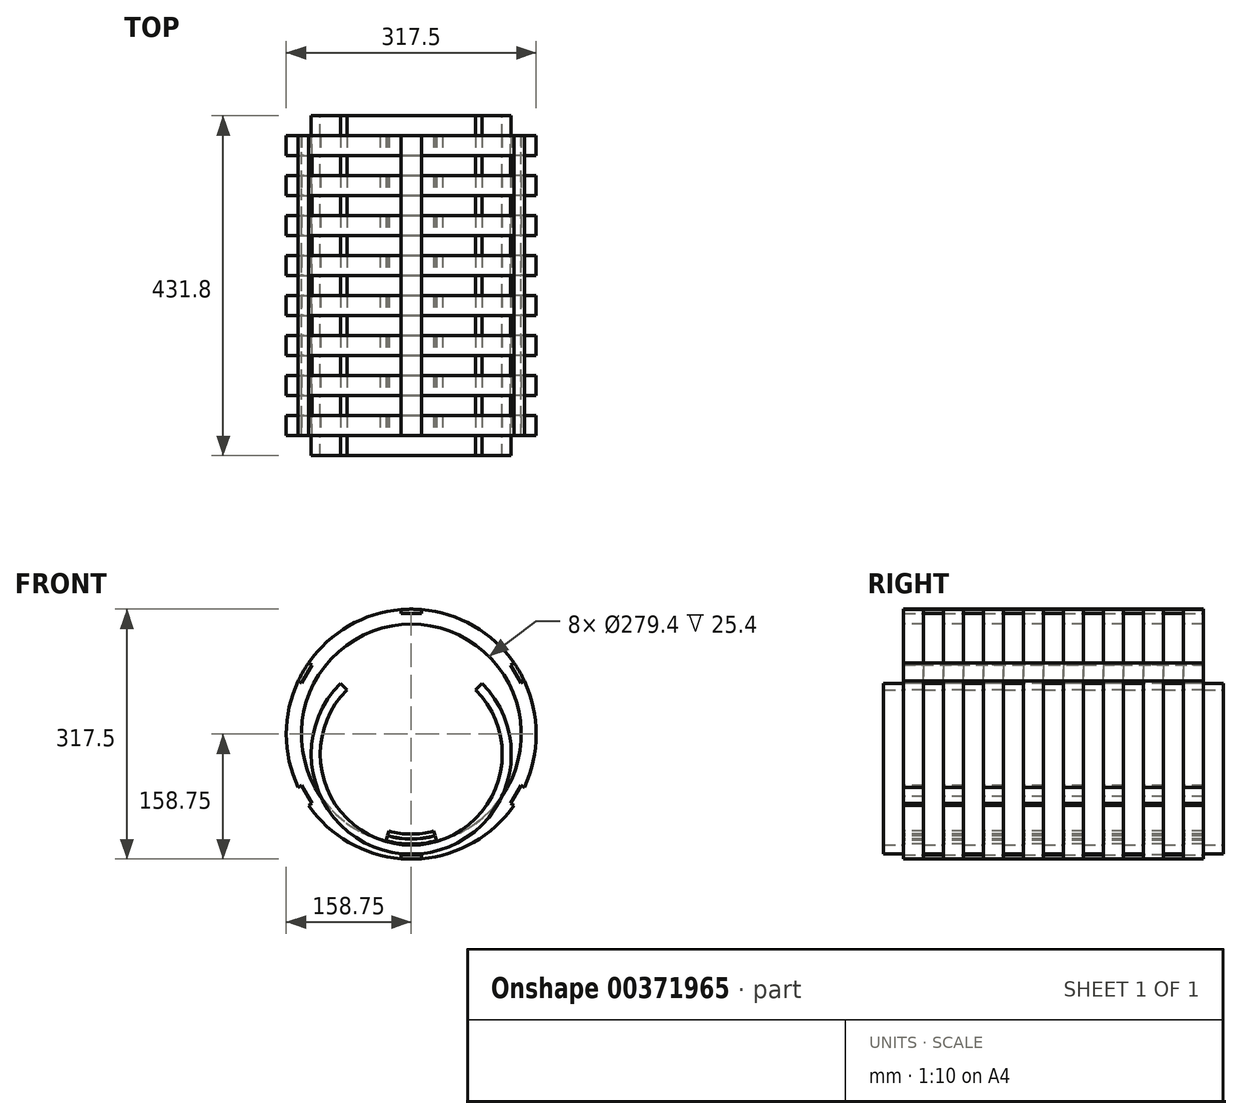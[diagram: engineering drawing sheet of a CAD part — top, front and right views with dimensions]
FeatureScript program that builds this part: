
annotation { "Feature Type Name" : "Feature", "Feature Type Description" : "" }
export const myFeature = defineFeature(function(context is Context, id is Id, definition is map)
    precondition{}
    {
        {
            var Q0;
            Q0=qCreatedBy(makeId("Front.planeOp"),FACE);
            var sketch = newSketch(context, id + "F0", { "sketchPlane" : qUnion([Q0])});
            skCircle(sketch, "E0", {"center": v(0, 0) * mm, "radius": 114.3 * mm});
            skCircle(sketch, "E1", {"center": v(0, 0) * mm, "radius": 107.95 * mm});
            skCircle(sketch, "E2", {"center": v(0, 0) * mm, "radius": 107.63 * mm});
            skCircle(sketch, "E3", {"center": v(0, 0) * mm, "radius": 101.6 * mm});
            skLineSegment(sketch, "E4", {"start": v(-28.5, -97.52) * mm, "end": v(-30.18, -103.31) * mm});
            skLineSegment(sketch, "E5", {"start": v(-30.27, -103.62) * mm, "end": v(-32.05, -109.71) * mm});
            skLineSegment(sketch, "E6", {"start": v(28.5, -97.52) * mm, "end": v(30.18, -103.31) * mm});
            skLineSegment(sketch, "E7", {"start": v(30.27, -103.62) * mm, "end": v(32.05, -109.71) * mm});
            skCircle(sketch, "E8", {"center": v(0, 0) * mm, "radius": 115.57 * mm});
            skCircle(sketch, "E9", {"center": v(0, 0) * mm, "radius": 127 * mm});
            skLineSegment(sketch, "E10", {"start": v(0, 0) * mm, "end": v(0, 68.07) * mm});
            skLineSegment(sketch, "E11", {"start": v(0, 0) * mm, "end": v(89.8, 89.8) * mm});
            skLineSegment(sketch, "E12", {"start": v(0, 0) * mm, "end": v(-89.8, 89.8) * mm});
            skCircle(sketch, "E13", {"center": v(0, 0) * mm, "radius": 139.7 * mm});
            skCircle(sketch, "E14", {"center": v(0, 0) * mm, "radius": 158.75 * mm});
            skLineSegment(sketch, "E15.bottom", {"start": v(13.23, 153.33) * mm, "end": v(-13.23, 153.33) * mm});
            skPoint(sketch, "E15.middle", {"position": v(0, 158.75) * mm});
            skArc(sketch, "E16", {"start": v(13.23, 158.2) * mm, "mid": v(0, 158.75) * mm, "end": v(-13.23, 158.2) * mm});
            skLineSegment(sketch, "E17", {"start": v(-13.23, 158.2) * mm, "end": v(-13.23, 153.33) * mm});
            skLineSegment(sketch, "E18", {"start": v(-13.23, 153.33) * mm, "end": v(13.23, 153.33) * mm});
            skLineSegment(sketch, "E19", {"start": v(13.23, 153.33) * mm, "end": v(13.23, 158.2) * mm});
            skLineSegment(sketch, "E20.1.0", {"start": v(-130.39, -90.56) * mm, "end": v(-126.17, -88.12) * mm});
            skLineSegment(sketch, "E20.1.1", {"start": v(-126.17, -88.12) * mm, "end": v(-139.4, -65.2) * mm});
            skLineSegment(sketch, "E20.1.2", {"start": v(-139.4, -65.2) * mm, "end": v(-143.62, -67.64) * mm});
            skLineSegment(sketch, "E20.2.0", {"start": v(143.62, -67.64) * mm, "end": v(139.4, -65.2) * mm});
            skLineSegment(sketch, "E20.2.1", {"start": v(139.4, -65.2) * mm, "end": v(126.17, -88.12) * mm});
            skLineSegment(sketch, "E20.2.2", {"start": v(126.17, -88.12) * mm, "end": v(130.39, -90.56) * mm});
            skArc(sketch, "E21.1.0", {"start": v(-130.39, 90.56) * mm, "mid": v(-137.48, 79.38) * mm, "end": v(-143.62, 67.64) * mm});
            skLineSegment(sketch, "E21.1.1", {"start": v(-126.17, 88.12) * mm, "end": v(-130.39, 90.56) * mm});
            skLineSegment(sketch, "E21.1.2", {"start": v(-139.4, 65.2) * mm, "end": v(-126.17, 88.12) * mm});
            skLineSegment(sketch, "E21.1.3", {"start": v(-143.62, 67.64) * mm, "end": v(-139.4, 65.2) * mm});
            skArc(sketch, "E21.2.0", {"start": v(-143.62, -67.64) * mm, "mid": v(-137.48, -79.38) * mm, "end": v(-130.39, -90.56) * mm});
            skArc(sketch, "E21.3.0", {"start": v(-13.23, -158.2) * mm, "mid": v(0, -158.75) * mm, "end": v(13.23, -158.2) * mm});
            skLineSegment(sketch, "E21.3.1", {"start": v(-13.23, -153.33) * mm, "end": v(-13.23, -158.2) * mm});
            skLineSegment(sketch, "E21.3.2", {"start": v(13.23, -153.33) * mm, "end": v(-13.23, -153.33) * mm});
            skLineSegment(sketch, "E21.3.3", {"start": v(13.23, -158.2) * mm, "end": v(13.23, -153.33) * mm});
            skArc(sketch, "E21.4.0", {"start": v(130.39, -90.56) * mm, "mid": v(137.48, -79.38) * mm, "end": v(143.62, -67.64) * mm});
            skArc(sketch, "E21.5.0", {"start": v(143.62, 67.64) * mm, "mid": v(137.48, 79.38) * mm, "end": v(130.39, 90.56) * mm});
            skLineSegment(sketch, "E21.5.1", {"start": v(139.4, 65.2) * mm, "end": v(143.62, 67.64) * mm});
            skLineSegment(sketch, "E21.5.2", {"start": v(126.17, 88.12) * mm, "end": v(139.4, 65.2) * mm});
            skLineSegment(sketch, "E21.5.3", {"start": v(130.39, 90.56) * mm, "end": v(126.17, 88.12) * mm});
            skCircle(sketch, "E22", {"center": v(0, 0) * mm, "radius": 25.4 * mm});
            skArc(sketch, "E23", {"start": v(-114.96, -53.97) * mm, "mid": v(0, -114.3) * mm, "end": v(114.96, -53.97) * mm});
            skSolve(sketch);
        }
        {
            var Q0;
            {var subQ0=sQuery(id+"F0.wireOp",EDGE,"E4");Q0=makeQuery(id+"F0.imprint","IMPRINT",FACE,{"disambiguationData":[TD([[makeQuery(id+"F0.imprint","IMPRINT",EDGE,{"derivedFrom":subQ0}),1.0]])]});}
            extrude(context, id + "F1", {"entities" : qUnion([Q0]), "oppositeDirection" : true, "depth" : 25.4 * mm, "offsetDistance" : 25.4 * mm});
        }
        {
            var Q0;
            {var subQ0=sQuery(id+"F0.wireOp",EDGE,"E5");Q0=makeQuery(id+"F0.imprint","IMPRINT",FACE,{"disambiguationData":[TD([[makeQuery(id+"F0.imprint","IMPRINT",EDGE,{"derivedFrom":subQ0}),1.0]])]});}
            extrude(context, id + "F2", {"entities" : qUnion([Q0]), "oppositeDirection" : true, "depth" : 25.4 * mm, "offsetDistance" : 25.4 * mm});
        }
        {
            var Q0;
            {var subQ0=sQuery(id+"F0.wireOp",EDGE,"E12");var subQ1=sQuery(id+"F0.wireOp",EDGE,"E8");var subQ2=makeQuery(id+"F0.imprint","INTERSECT",VERTEX,{"derivedFrom":[subQ1,subQ0]});Q0=makeQuery(id+"F0.imprint","IMPRINT",FACE,{"disambiguationData":[TD([[makeQuery(id+"F0.imprint","IMPRINT",EDGE,{"disambiguationData":[TD([[subQ2,-1.0]])],"derivedFrom":subQ1}),-1.0]])]});}
            var Q1;
            {var subQ0=sQuery(id+"F0.wireOp",EDGE,"E11");var subQ1=sQuery(id+"F0.wireOp",EDGE,"E8");var subQ2=makeQuery(id+"F0.imprint","INTERSECT",VERTEX,{"derivedFrom":[subQ1,subQ0]});Q1=makeQuery(id+"F0.imprint","IMPRINT",FACE,{"disambiguationData":[TD([[makeQuery(id+"F0.imprint","IMPRINT",EDGE,{"disambiguationData":[TD([[subQ2,1.0]])],"derivedFrom":subQ1}),-1.0]])]});}
            extrude(context, id + "F3", {"entities" : qUnion([Q0, Q1]), "oppositeDirection" : true, "depth" : 25.4 * mm, "offsetDistance" : 25.4 * mm});
        }
        {
            var Q0;
            Q0=makeQuery(id+"F0.imprint","IMPRINT",FACE,{"disambiguationData":[TD([[makeQuery(id+"F0.imprint","IMPRINT",EDGE,{"derivedFrom":sQuery(id+"F0.wireOp",EDGE,"E13")}),-1.0]])]});
            extrude(context, id + "F4", {"entities" : qUnion([Q0]), "oppositeDirection" : true, "depth" : 25.4 * mm, "offsetDistance" : 25.4 * mm});
        }
        {
            var Q0;
            Q0=makeQuery(id+"F4.opExtrude","SWEPT_BODY",BODY,{"disambiguationData":[OSD([sQuery(id+"F0.wireOp",EDGE,"E13"),sQuery(id+"F0.wireOp",EDGE,"E14"),sQuery(id+"F0.wireOp",EDGE,"E17"),sQuery(id+"F0.wireOp",EDGE,"E18"),sQuery(id+"F0.wireOp",EDGE,"E19"),sQuery(id+"F0.wireOp",EDGE,"E21.1.1"),sQuery(id+"F0.wireOp",EDGE,"E21.1.2"),sQuery(id+"F0.wireOp",EDGE,"E21.1.3"),sQuery(id+"F0.wireOp",EDGE,"E20.1.2"),sQuery(id+"F0.wireOp",EDGE,"E20.1.1"),sQuery(id+"F0.wireOp",EDGE,"E20.1.0"),sQuery(id+"F0.wireOp",EDGE,"E21.3.1"),sQuery(id+"F0.wireOp",EDGE,"E21.3.2"),sQuery(id+"F0.wireOp",EDGE,"E21.3.3"),sQuery(id+"F0.wireOp",EDGE,"E20.2.2"),sQuery(id+"F0.wireOp",EDGE,"E20.2.1"),sQuery(id+"F0.wireOp",EDGE,"E20.2.0"),sQuery(id+"F0.wireOp",EDGE,"E21.5.1"),sQuery(id+"F0.wireOp",EDGE,"E21.5.2"),sQuery(id+"F0.wireOp",EDGE,"E21.5.3")])]});
            transform(context, id + "F5", {"entities" : qUnion([Q0]), "transformType" : TransformType.TRANSLATION_3D, "dx" : 0 * mm, "dy" : 0 * mm, "dz" : 25.4 * mm, "makeCopy" : false});
        }
        {
            var Q0;
            {var subQ0=sQuery(id+"F0.wireOp",EDGE,"E12");var subQ1=sQuery(id+"F0.wireOp",EDGE,"E8");var subQ2=makeQuery(id+"F0.imprint","INTERSECT",VERTEX,{"derivedFrom":[subQ1,subQ0]});Q0=makeQuery(id+"F0.imprint","IMPRINT",FACE,{"disambiguationData":[TD([[makeQuery(id+"F0.imprint","IMPRINT",EDGE,{"disambiguationData":[TD([[subQ2,-1.0]])],"derivedFrom":subQ1}),-1.0]])]});}
            var Q1;
            {var subQ0=sQuery(id+"F0.wireOp",EDGE,"E11");var subQ1=sQuery(id+"F0.wireOp",EDGE,"E8");var subQ2=makeQuery(id+"F0.imprint","INTERSECT",VERTEX,{"derivedFrom":[subQ1,subQ0]});Q1=makeQuery(id+"F0.imprint","IMPRINT",FACE,{"disambiguationData":[TD([[makeQuery(id+"F0.imprint","IMPRINT",EDGE,{"disambiguationData":[TD([[subQ2,1.0]])],"derivedFrom":subQ1}),-1.0]])]});}
            var Q2;
            {var subQ0=sQuery(id+"F0.wireOp",EDGE,"E23");var subQ1=sQuery(id+"F0.wireOp",EDGE,"E8");var subQ2=makeQuery(id+"F0.imprint","INTERSECT",VERTEX,{"disambiguationData":[OD(0.0)],"derivedFrom":[subQ1,subQ0]});Q2=makeQuery(id+"F0.imprint","IMPRINT",FACE,{"disambiguationData":[TD([[makeQuery(id+"F0.imprint","IMPRINT",EDGE,{"disambiguationData":[TD([[subQ2,-1.0]])],"derivedFrom":subQ1}),-1.0]])]});}
            extrude(context, id + "F6", {"entities" : qUnion([Q0, Q1, Q2]), "depth" : 25.4 * mm, "offsetDistance" : 25.4 * mm});
        }
        {
            var Q0;
            {var subQ0=sQuery(id+"F0.wireOp",EDGE,"E21.5.1");Q0=makeQuery(id+"F0.imprint","IMPRINT",FACE,{"disambiguationData":[TD([[makeQuery(id+"F0.imprint","IMPRINT",EDGE,{"derivedFrom":subQ0}),1.0]])]});}
            var Q1;
            {var subQ0=sQuery(id+"F0.wireOp",EDGE,"E17");Q1=makeQuery(id+"F0.imprint","IMPRINT",FACE,{"disambiguationData":[TD([[makeQuery(id+"F0.imprint","IMPRINT",EDGE,{"derivedFrom":subQ0}),1.0]])]});}
            var Q2;
            {var subQ0=sQuery(id+"F0.wireOp",EDGE,"E21.1.1");Q2=makeQuery(id+"F0.imprint","IMPRINT",FACE,{"disambiguationData":[TD([[makeQuery(id+"F0.imprint","IMPRINT",EDGE,{"derivedFrom":subQ0}),1.0]])]});}
            var Q3;
            {var subQ0=sQuery(id+"F0.wireOp",EDGE,"E21.3.1");Q3=makeQuery(id+"F0.imprint","IMPRINT",FACE,{"disambiguationData":[TD([[makeQuery(id+"F0.imprint","IMPRINT",EDGE,{"derivedFrom":subQ0}),1.0]])]});}
            var Q4;
            {var subQ0=sQuery(id+"F0.wireOp",EDGE,"E20.1.2");Q4=makeQuery(id+"F0.imprint","IMPRINT",FACE,{"disambiguationData":[TD([[makeQuery(id+"F0.imprint","IMPRINT",EDGE,{"derivedFrom":subQ0}),1.0]])]});}
            var Q5;
            {var subQ0=sQuery(id+"F0.wireOp",EDGE,"E20.2.2");Q5=makeQuery(id+"F0.imprint","IMPRINT",FACE,{"disambiguationData":[TD([[makeQuery(id+"F0.imprint","IMPRINT",EDGE,{"derivedFrom":subQ0}),1.0]])]});}
            extrude(context, id + "F7", {"entities" : qUnion([Q0, Q1, Q2, Q3, Q4, Q5]), "depth" : 381 * mm, "offsetDistance" : 25.4 * mm});
        }
        {
            var Q0;
            Q0=makeQuery(id+"F7.opExtrude","SWEPT_BODY",BODY,{"disambiguationData":[OSD([sQuery(id+"F0.wireOp",EDGE,"E14"),sQuery(id+"F0.wireOp",EDGE,"E21.1.1"),sQuery(id+"F0.wireOp",EDGE,"E21.1.2"),sQuery(id+"F0.wireOp",EDGE,"E21.1.3")])]});
            var Q1;
            Q1=makeQuery(id+"F7.opExtrude","SWEPT_BODY",BODY,{"disambiguationData":[OSD([sQuery(id+"F0.wireOp",EDGE,"E14"),sQuery(id+"F0.wireOp",EDGE,"E17"),sQuery(id+"F0.wireOp",EDGE,"E18"),sQuery(id+"F0.wireOp",EDGE,"E19")])]});
            var Q2;
            Q2=makeQuery(id+"F7.opExtrude","SWEPT_BODY",BODY,{"disambiguationData":[OSD([sQuery(id+"F0.wireOp",EDGE,"E14"),sQuery(id+"F0.wireOp",EDGE,"E21.5.1"),sQuery(id+"F0.wireOp",EDGE,"E21.5.2"),sQuery(id+"F0.wireOp",EDGE,"E21.5.3")])]});
            var Q3;
            Q3=makeQuery(id+"F7.opExtrude","SWEPT_BODY",BODY,{"disambiguationData":[OSD([sQuery(id+"F0.wireOp",EDGE,"E14"),sQuery(id+"F0.wireOp",EDGE,"E20.1.2"),sQuery(id+"F0.wireOp",EDGE,"E20.1.1"),sQuery(id+"F0.wireOp",EDGE,"E20.1.0")])]});
            var Q4;
            Q4=makeQuery(id+"F7.opExtrude","SWEPT_BODY",BODY,{"disambiguationData":[OSD([sQuery(id+"F0.wireOp",EDGE,"E14"),sQuery(id+"F0.wireOp",EDGE,"E21.3.1"),sQuery(id+"F0.wireOp",EDGE,"E21.3.2"),sQuery(id+"F0.wireOp",EDGE,"E21.3.3")])]});
            var Q5;
            Q5=makeQuery(id+"F7.opExtrude","SWEPT_BODY",BODY,{"disambiguationData":[OSD([sQuery(id+"F0.wireOp",EDGE,"E14"),sQuery(id+"F0.wireOp",EDGE,"E20.2.2"),sQuery(id+"F0.wireOp",EDGE,"E20.2.1"),sQuery(id+"F0.wireOp",EDGE,"E20.2.0")])]});
            transform(context, id + "F8", {"entities" : qUnion([Q0, Q1, Q2, Q3, Q4, Q5]), "transformType" : TransformType.TRANSLATION_3D, "dx" : 0 * mm, "dy" : 381 * mm, "dz" : 25.4 * mm, "makeCopy" : false});
        }
        {
            var Q0;
            Q0=makeQuery(id+"F6.opExtrude","SWEPT_BODY",BODY,{"disambiguationData":[OSD([sQuery(id+"F0.wireOp",EDGE,"E8"),sQuery(id+"F0.wireOp",EDGE,"E9"),sQuery(id+"F0.wireOp",EDGE,"E11"),sQuery(id+"F0.wireOp",EDGE,"E12")])]});
            var Q1;
            Q1=makeQuery(id+"F3.opExtrude","SWEPT_BODY",BODY,{"disambiguationData":[OSD([sQuery(id+"F0.wireOp",EDGE,"E8"),sQuery(id+"F0.wireOp",EDGE,"E9"),sQuery(id+"F0.wireOp",EDGE,"E12"),sQuery(id+"F0.wireOp",EDGE,"E23")])]});
            var Q2;
            Q2=makeQuery(id+"F3.opExtrude","SWEPT_BODY",BODY,{"disambiguationData":[OSD([sQuery(id+"F0.wireOp",EDGE,"E8"),sQuery(id+"F0.wireOp",EDGE,"E9"),sQuery(id+"F0.wireOp",EDGE,"E11"),sQuery(id+"F0.wireOp",EDGE,"E23")])]});
            var Q3;
            Q3=makeQuery(id+"F4.opExtrude","SWEPT_BODY",BODY,{"disambiguationData":[OSD([sQuery(id+"F0.wireOp",EDGE,"E13"),sQuery(id+"F0.wireOp",EDGE,"E14"),sQuery(id+"F0.wireOp",EDGE,"E17"),sQuery(id+"F0.wireOp",EDGE,"E18"),sQuery(id+"F0.wireOp",EDGE,"E19"),sQuery(id+"F0.wireOp",EDGE,"E21.1.1"),sQuery(id+"F0.wireOp",EDGE,"E21.1.2"),sQuery(id+"F0.wireOp",EDGE,"E21.1.3"),sQuery(id+"F0.wireOp",EDGE,"E20.1.2"),sQuery(id+"F0.wireOp",EDGE,"E20.1.1"),sQuery(id+"F0.wireOp",EDGE,"E20.1.0"),sQuery(id+"F0.wireOp",EDGE,"E21.3.1"),sQuery(id+"F0.wireOp",EDGE,"E21.3.2"),sQuery(id+"F0.wireOp",EDGE,"E21.3.3"),sQuery(id+"F0.wireOp",EDGE,"E20.2.2"),sQuery(id+"F0.wireOp",EDGE,"E20.2.1"),sQuery(id+"F0.wireOp",EDGE,"E20.2.0"),sQuery(id+"F0.wireOp",EDGE,"E21.5.1"),sQuery(id+"F0.wireOp",EDGE,"E21.5.2"),sQuery(id+"F0.wireOp",EDGE,"E21.5.3")])]});
            var Q4;
            Q4=makeQuery(id+"F1.opExtrude","SWEPT_BODY",BODY,{"disambiguationData":[OSD([sQuery(id+"F0.wireOp",EDGE,"E2"),sQuery(id+"F0.wireOp",EDGE,"E3"),sQuery(id+"F0.wireOp",EDGE,"E4"),sQuery(id+"F0.wireOp",EDGE,"E6")])]});
            var Q5;
            Q5=makeQuery(id+"F2.opExtrude","SWEPT_BODY",BODY,{"disambiguationData":[OSD([sQuery(id+"F0.wireOp",EDGE,"E0"),sQuery(id+"F0.wireOp",EDGE,"E1"),sQuery(id+"F0.wireOp",EDGE,"E5"),sQuery(id+"F0.wireOp",EDGE,"E7")])]});
            transform(context, id + "F9", {"entities" : qUnion([Q0, Q1, Q2, Q3, Q4, Q5]), "transformType" : TransformType.TRANSLATION_3D, "dx" : 0 * mm, "dy" : 50.8 * mm, "dz" : 0 * mm, "makeCopy" : true});
        }
        {
            var Q0;
            Q0=makeQuery(id+"F6.opExtrude","SWEPT_BODY",BODY,{"disambiguationData":[OSD([sQuery(id+"F0.wireOp",EDGE,"E8"),sQuery(id+"F0.wireOp",EDGE,"E9"),sQuery(id+"F0.wireOp",EDGE,"E11"),sQuery(id+"F0.wireOp",EDGE,"E12")])]});
            var Q1;
            Q1=makeQuery(id+"F3.opExtrude","SWEPT_BODY",BODY,{"disambiguationData":[OSD([sQuery(id+"F0.wireOp",EDGE,"E8"),sQuery(id+"F0.wireOp",EDGE,"E9"),sQuery(id+"F0.wireOp",EDGE,"E12"),sQuery(id+"F0.wireOp",EDGE,"E23")])]});
            var Q2;
            Q2=makeQuery(id+"F3.opExtrude","SWEPT_BODY",BODY,{"disambiguationData":[OSD([sQuery(id+"F0.wireOp",EDGE,"E8"),sQuery(id+"F0.wireOp",EDGE,"E9"),sQuery(id+"F0.wireOp",EDGE,"E11"),sQuery(id+"F0.wireOp",EDGE,"E23")])]});
            var Q3;
            Q3=makeQuery(id+"F9.opPattern","COPY",BODY,{"derivedFrom":makeQuery(id+"F6.opExtrude","SWEPT_BODY",BODY,{"disambiguationData":[OSD([sQuery(id+"F0.wireOp",EDGE,"E8"),sQuery(id+"F0.wireOp",EDGE,"E9"),sQuery(id+"F0.wireOp",EDGE,"E11"),sQuery(id+"F0.wireOp",EDGE,"E12")])]}),"instanceName":"1"});
            var Q4;
            Q4=makeQuery(id+"F9.opPattern","COPY",BODY,{"derivedFrom":makeQuery(id+"F3.opExtrude","SWEPT_BODY",BODY,{"disambiguationData":[OSD([sQuery(id+"F0.wireOp",EDGE,"E8"),sQuery(id+"F0.wireOp",EDGE,"E9"),sQuery(id+"F0.wireOp",EDGE,"E12"),sQuery(id+"F0.wireOp",EDGE,"E23")])]}),"instanceName":"1"});
            var Q5;
            Q5=makeQuery(id+"F9.opPattern","COPY",BODY,{"derivedFrom":makeQuery(id+"F3.opExtrude","SWEPT_BODY",BODY,{"disambiguationData":[OSD([sQuery(id+"F0.wireOp",EDGE,"E8"),sQuery(id+"F0.wireOp",EDGE,"E9"),sQuery(id+"F0.wireOp",EDGE,"E11"),sQuery(id+"F0.wireOp",EDGE,"E23")])]}),"instanceName":"1"});
            var Q6;
            Q6=makeQuery(id+"F4.opExtrude","SWEPT_BODY",BODY,{"disambiguationData":[OSD([sQuery(id+"F0.wireOp",EDGE,"E13"),sQuery(id+"F0.wireOp",EDGE,"E14"),sQuery(id+"F0.wireOp",EDGE,"E17"),sQuery(id+"F0.wireOp",EDGE,"E18"),sQuery(id+"F0.wireOp",EDGE,"E19"),sQuery(id+"F0.wireOp",EDGE,"E21.1.1"),sQuery(id+"F0.wireOp",EDGE,"E21.1.2"),sQuery(id+"F0.wireOp",EDGE,"E21.1.3"),sQuery(id+"F0.wireOp",EDGE,"E20.1.2"),sQuery(id+"F0.wireOp",EDGE,"E20.1.1"),sQuery(id+"F0.wireOp",EDGE,"E20.1.0"),sQuery(id+"F0.wireOp",EDGE,"E21.3.1"),sQuery(id+"F0.wireOp",EDGE,"E21.3.2"),sQuery(id+"F0.wireOp",EDGE,"E21.3.3"),sQuery(id+"F0.wireOp",EDGE,"E20.2.2"),sQuery(id+"F0.wireOp",EDGE,"E20.2.1"),sQuery(id+"F0.wireOp",EDGE,"E20.2.0"),sQuery(id+"F0.wireOp",EDGE,"E21.5.1"),sQuery(id+"F0.wireOp",EDGE,"E21.5.2"),sQuery(id+"F0.wireOp",EDGE,"E21.5.3")])]});
            var Q7;
            Q7=makeQuery(id+"F9.opPattern","COPY",BODY,{"derivedFrom":makeQuery(id+"F4.opExtrude","SWEPT_BODY",BODY,{"disambiguationData":[OSD([sQuery(id+"F0.wireOp",EDGE,"E13"),sQuery(id+"F0.wireOp",EDGE,"E14"),sQuery(id+"F0.wireOp",EDGE,"E17"),sQuery(id+"F0.wireOp",EDGE,"E18"),sQuery(id+"F0.wireOp",EDGE,"E19"),sQuery(id+"F0.wireOp",EDGE,"E21.1.1"),sQuery(id+"F0.wireOp",EDGE,"E21.1.2"),sQuery(id+"F0.wireOp",EDGE,"E21.1.3"),sQuery(id+"F0.wireOp",EDGE,"E20.1.2"),sQuery(id+"F0.wireOp",EDGE,"E20.1.1"),sQuery(id+"F0.wireOp",EDGE,"E20.1.0"),sQuery(id+"F0.wireOp",EDGE,"E21.3.1"),sQuery(id+"F0.wireOp",EDGE,"E21.3.2"),sQuery(id+"F0.wireOp",EDGE,"E21.3.3"),sQuery(id+"F0.wireOp",EDGE,"E20.2.2"),sQuery(id+"F0.wireOp",EDGE,"E20.2.1"),sQuery(id+"F0.wireOp",EDGE,"E20.2.0"),sQuery(id+"F0.wireOp",EDGE,"E21.5.1"),sQuery(id+"F0.wireOp",EDGE,"E21.5.2"),sQuery(id+"F0.wireOp",EDGE,"E21.5.3")])]}),"instanceName":"1"});
            var Q8;
            Q8=makeQuery(id+"F1.opExtrude","SWEPT_BODY",BODY,{"disambiguationData":[OSD([sQuery(id+"F0.wireOp",EDGE,"E2"),sQuery(id+"F0.wireOp",EDGE,"E3"),sQuery(id+"F0.wireOp",EDGE,"E4"),sQuery(id+"F0.wireOp",EDGE,"E6")])]});
            var Q9;
            Q9=makeQuery(id+"F2.opExtrude","SWEPT_BODY",BODY,{"disambiguationData":[OSD([sQuery(id+"F0.wireOp",EDGE,"E0"),sQuery(id+"F0.wireOp",EDGE,"E1"),sQuery(id+"F0.wireOp",EDGE,"E5"),sQuery(id+"F0.wireOp",EDGE,"E7")])]});
            var Q10;
            Q10=makeQuery(id+"F9.opPattern","COPY",BODY,{"derivedFrom":makeQuery(id+"F1.opExtrude","SWEPT_BODY",BODY,{"disambiguationData":[OSD([sQuery(id+"F0.wireOp",EDGE,"E2"),sQuery(id+"F0.wireOp",EDGE,"E3"),sQuery(id+"F0.wireOp",EDGE,"E4"),sQuery(id+"F0.wireOp",EDGE,"E6")])]}),"instanceName":"1"});
            var Q11;
            Q11=makeQuery(id+"F9.opPattern","COPY",BODY,{"derivedFrom":makeQuery(id+"F2.opExtrude","SWEPT_BODY",BODY,{"disambiguationData":[OSD([sQuery(id+"F0.wireOp",EDGE,"E0"),sQuery(id+"F0.wireOp",EDGE,"E1"),sQuery(id+"F0.wireOp",EDGE,"E5"),sQuery(id+"F0.wireOp",EDGE,"E7")])]}),"instanceName":"1"});
            transform(context, id + "F10", {"entities" : qUnion([Q0, Q1, Q2, Q3, Q4, Q5, Q6, Q7, Q8, Q9, Q10, Q11]), "transformType" : TransformType.TRANSLATION_3D, "dx" : 0 * mm, "dy" : 101.6 * mm, "dz" : 0 * mm, "makeCopy" : true});
        }
        {
            var Q0;
            Q0=makeQuery(id+"F6.opExtrude","SWEPT_BODY",BODY,{"disambiguationData":[OSD([sQuery(id+"F0.wireOp",EDGE,"E8"),sQuery(id+"F0.wireOp",EDGE,"E9"),sQuery(id+"F0.wireOp",EDGE,"E11"),sQuery(id+"F0.wireOp",EDGE,"E12")])]});
            var Q1;
            Q1=makeQuery(id+"F3.opExtrude","SWEPT_BODY",BODY,{"disambiguationData":[OSD([sQuery(id+"F0.wireOp",EDGE,"E8"),sQuery(id+"F0.wireOp",EDGE,"E9"),sQuery(id+"F0.wireOp",EDGE,"E12"),sQuery(id+"F0.wireOp",EDGE,"E23")])]});
            var Q2;
            Q2=makeQuery(id+"F3.opExtrude","SWEPT_BODY",BODY,{"disambiguationData":[OSD([sQuery(id+"F0.wireOp",EDGE,"E8"),sQuery(id+"F0.wireOp",EDGE,"E9"),sQuery(id+"F0.wireOp",EDGE,"E11"),sQuery(id+"F0.wireOp",EDGE,"E23")])]});
            var Q3;
            Q3=makeQuery(id+"F9.opPattern","COPY",BODY,{"derivedFrom":makeQuery(id+"F6.opExtrude","SWEPT_BODY",BODY,{"disambiguationData":[OSD([sQuery(id+"F0.wireOp",EDGE,"E8"),sQuery(id+"F0.wireOp",EDGE,"E9"),sQuery(id+"F0.wireOp",EDGE,"E11"),sQuery(id+"F0.wireOp",EDGE,"E12")])]}),"instanceName":"1"});
            var Q4;
            Q4=makeQuery(id+"F9.opPattern","COPY",BODY,{"derivedFrom":makeQuery(id+"F3.opExtrude","SWEPT_BODY",BODY,{"disambiguationData":[OSD([sQuery(id+"F0.wireOp",EDGE,"E8"),sQuery(id+"F0.wireOp",EDGE,"E9"),sQuery(id+"F0.wireOp",EDGE,"E11"),sQuery(id+"F0.wireOp",EDGE,"E23")])]}),"instanceName":"1"});
            var Q5;
            Q5=makeQuery(id+"F9.opPattern","COPY",BODY,{"derivedFrom":makeQuery(id+"F3.opExtrude","SWEPT_BODY",BODY,{"disambiguationData":[OSD([sQuery(id+"F0.wireOp",EDGE,"E8"),sQuery(id+"F0.wireOp",EDGE,"E9"),sQuery(id+"F0.wireOp",EDGE,"E12"),sQuery(id+"F0.wireOp",EDGE,"E23")])]}),"instanceName":"1"});
            var Q6;
            Q6=makeQuery(id+"F10.opPattern","COPY",BODY,{"derivedFrom":makeQuery(id+"F6.opExtrude","SWEPT_BODY",BODY,{"disambiguationData":[OSD([sQuery(id+"F0.wireOp",EDGE,"E8"),sQuery(id+"F0.wireOp",EDGE,"E9"),sQuery(id+"F0.wireOp",EDGE,"E11"),sQuery(id+"F0.wireOp",EDGE,"E12")])]}),"instanceName":"1"});
            var Q7;
            Q7=makeQuery(id+"F10.opPattern","COPY",BODY,{"derivedFrom":makeQuery(id+"F3.opExtrude","SWEPT_BODY",BODY,{"disambiguationData":[OSD([sQuery(id+"F0.wireOp",EDGE,"E8"),sQuery(id+"F0.wireOp",EDGE,"E9"),sQuery(id+"F0.wireOp",EDGE,"E12"),sQuery(id+"F0.wireOp",EDGE,"E23")])]}),"instanceName":"1"});
            var Q8;
            Q8=makeQuery(id+"F10.opPattern","COPY",BODY,{"derivedFrom":makeQuery(id+"F3.opExtrude","SWEPT_BODY",BODY,{"disambiguationData":[OSD([sQuery(id+"F0.wireOp",EDGE,"E8"),sQuery(id+"F0.wireOp",EDGE,"E9"),sQuery(id+"F0.wireOp",EDGE,"E11"),sQuery(id+"F0.wireOp",EDGE,"E23")])]}),"instanceName":"1"});
            var Q9;
            Q9=makeQuery(id+"F10.opPattern","COPY",BODY,{"derivedFrom":makeQuery(id+"F9.opPattern","COPY",BODY,{"derivedFrom":makeQuery(id+"F6.opExtrude","SWEPT_BODY",BODY,{"disambiguationData":[OSD([sQuery(id+"F0.wireOp",EDGE,"E8"),sQuery(id+"F0.wireOp",EDGE,"E9"),sQuery(id+"F0.wireOp",EDGE,"E11"),sQuery(id+"F0.wireOp",EDGE,"E12")])]}),"instanceName":"1"}),"instanceName":"1"});
            var Q10;
            Q10=makeQuery(id+"F10.opPattern","COPY",BODY,{"derivedFrom":makeQuery(id+"F9.opPattern","COPY",BODY,{"derivedFrom":makeQuery(id+"F3.opExtrude","SWEPT_BODY",BODY,{"disambiguationData":[OSD([sQuery(id+"F0.wireOp",EDGE,"E8"),sQuery(id+"F0.wireOp",EDGE,"E9"),sQuery(id+"F0.wireOp",EDGE,"E11"),sQuery(id+"F0.wireOp",EDGE,"E23")])]}),"instanceName":"1"}),"instanceName":"1"});
            var Q11;
            Q11=makeQuery(id+"F10.opPattern","COPY",BODY,{"derivedFrom":makeQuery(id+"F9.opPattern","COPY",BODY,{"derivedFrom":makeQuery(id+"F3.opExtrude","SWEPT_BODY",BODY,{"disambiguationData":[OSD([sQuery(id+"F0.wireOp",EDGE,"E8"),sQuery(id+"F0.wireOp",EDGE,"E9"),sQuery(id+"F0.wireOp",EDGE,"E12"),sQuery(id+"F0.wireOp",EDGE,"E23")])]}),"instanceName":"1"}),"instanceName":"1"});
            var Q12;
            Q12=makeQuery(id+"F4.opExtrude","SWEPT_BODY",BODY,{"disambiguationData":[OSD([sQuery(id+"F0.wireOp",EDGE,"E13"),sQuery(id+"F0.wireOp",EDGE,"E14"),sQuery(id+"F0.wireOp",EDGE,"E17"),sQuery(id+"F0.wireOp",EDGE,"E18"),sQuery(id+"F0.wireOp",EDGE,"E19"),sQuery(id+"F0.wireOp",EDGE,"E21.1.1"),sQuery(id+"F0.wireOp",EDGE,"E21.1.2"),sQuery(id+"F0.wireOp",EDGE,"E21.1.3"),sQuery(id+"F0.wireOp",EDGE,"E20.1.2"),sQuery(id+"F0.wireOp",EDGE,"E20.1.1"),sQuery(id+"F0.wireOp",EDGE,"E20.1.0"),sQuery(id+"F0.wireOp",EDGE,"E21.3.1"),sQuery(id+"F0.wireOp",EDGE,"E21.3.2"),sQuery(id+"F0.wireOp",EDGE,"E21.3.3"),sQuery(id+"F0.wireOp",EDGE,"E20.2.2"),sQuery(id+"F0.wireOp",EDGE,"E20.2.1"),sQuery(id+"F0.wireOp",EDGE,"E20.2.0"),sQuery(id+"F0.wireOp",EDGE,"E21.5.1"),sQuery(id+"F0.wireOp",EDGE,"E21.5.2"),sQuery(id+"F0.wireOp",EDGE,"E21.5.3")])]});
            var Q13;
            Q13=makeQuery(id+"F9.opPattern","COPY",BODY,{"derivedFrom":makeQuery(id+"F4.opExtrude","SWEPT_BODY",BODY,{"disambiguationData":[OSD([sQuery(id+"F0.wireOp",EDGE,"E13"),sQuery(id+"F0.wireOp",EDGE,"E14"),sQuery(id+"F0.wireOp",EDGE,"E17"),sQuery(id+"F0.wireOp",EDGE,"E18"),sQuery(id+"F0.wireOp",EDGE,"E19"),sQuery(id+"F0.wireOp",EDGE,"E21.1.1"),sQuery(id+"F0.wireOp",EDGE,"E21.1.2"),sQuery(id+"F0.wireOp",EDGE,"E21.1.3"),sQuery(id+"F0.wireOp",EDGE,"E20.1.2"),sQuery(id+"F0.wireOp",EDGE,"E20.1.1"),sQuery(id+"F0.wireOp",EDGE,"E20.1.0"),sQuery(id+"F0.wireOp",EDGE,"E21.3.1"),sQuery(id+"F0.wireOp",EDGE,"E21.3.2"),sQuery(id+"F0.wireOp",EDGE,"E21.3.3"),sQuery(id+"F0.wireOp",EDGE,"E20.2.2"),sQuery(id+"F0.wireOp",EDGE,"E20.2.1"),sQuery(id+"F0.wireOp",EDGE,"E20.2.0"),sQuery(id+"F0.wireOp",EDGE,"E21.5.1"),sQuery(id+"F0.wireOp",EDGE,"E21.5.2"),sQuery(id+"F0.wireOp",EDGE,"E21.5.3")])]}),"instanceName":"1"});
            var Q14;
            Q14=makeQuery(id+"F10.opPattern","COPY",BODY,{"derivedFrom":makeQuery(id+"F4.opExtrude","SWEPT_BODY",BODY,{"disambiguationData":[OSD([sQuery(id+"F0.wireOp",EDGE,"E13"),sQuery(id+"F0.wireOp",EDGE,"E14"),sQuery(id+"F0.wireOp",EDGE,"E17"),sQuery(id+"F0.wireOp",EDGE,"E18"),sQuery(id+"F0.wireOp",EDGE,"E19"),sQuery(id+"F0.wireOp",EDGE,"E21.1.1"),sQuery(id+"F0.wireOp",EDGE,"E21.1.2"),sQuery(id+"F0.wireOp",EDGE,"E21.1.3"),sQuery(id+"F0.wireOp",EDGE,"E20.1.2"),sQuery(id+"F0.wireOp",EDGE,"E20.1.1"),sQuery(id+"F0.wireOp",EDGE,"E20.1.0"),sQuery(id+"F0.wireOp",EDGE,"E21.3.1"),sQuery(id+"F0.wireOp",EDGE,"E21.3.2"),sQuery(id+"F0.wireOp",EDGE,"E21.3.3"),sQuery(id+"F0.wireOp",EDGE,"E20.2.2"),sQuery(id+"F0.wireOp",EDGE,"E20.2.1"),sQuery(id+"F0.wireOp",EDGE,"E20.2.0"),sQuery(id+"F0.wireOp",EDGE,"E21.5.1"),sQuery(id+"F0.wireOp",EDGE,"E21.5.2"),sQuery(id+"F0.wireOp",EDGE,"E21.5.3")])]}),"instanceName":"1"});
            var Q15;
            Q15=makeQuery(id+"F10.opPattern","COPY",BODY,{"derivedFrom":makeQuery(id+"F9.opPattern","COPY",BODY,{"derivedFrom":makeQuery(id+"F4.opExtrude","SWEPT_BODY",BODY,{"disambiguationData":[OSD([sQuery(id+"F0.wireOp",EDGE,"E13"),sQuery(id+"F0.wireOp",EDGE,"E14"),sQuery(id+"F0.wireOp",EDGE,"E17"),sQuery(id+"F0.wireOp",EDGE,"E18"),sQuery(id+"F0.wireOp",EDGE,"E19"),sQuery(id+"F0.wireOp",EDGE,"E21.1.1"),sQuery(id+"F0.wireOp",EDGE,"E21.1.2"),sQuery(id+"F0.wireOp",EDGE,"E21.1.3"),sQuery(id+"F0.wireOp",EDGE,"E20.1.2"),sQuery(id+"F0.wireOp",EDGE,"E20.1.1"),sQuery(id+"F0.wireOp",EDGE,"E20.1.0"),sQuery(id+"F0.wireOp",EDGE,"E21.3.1"),sQuery(id+"F0.wireOp",EDGE,"E21.3.2"),sQuery(id+"F0.wireOp",EDGE,"E21.3.3"),sQuery(id+"F0.wireOp",EDGE,"E20.2.2"),sQuery(id+"F0.wireOp",EDGE,"E20.2.1"),sQuery(id+"F0.wireOp",EDGE,"E20.2.0"),sQuery(id+"F0.wireOp",EDGE,"E21.5.1"),sQuery(id+"F0.wireOp",EDGE,"E21.5.2"),sQuery(id+"F0.wireOp",EDGE,"E21.5.3")])]}),"instanceName":"1"}),"instanceName":"1"});
            var Q16;
            Q16=makeQuery(id+"F1.opExtrude","SWEPT_BODY",BODY,{"disambiguationData":[OSD([sQuery(id+"F0.wireOp",EDGE,"E2"),sQuery(id+"F0.wireOp",EDGE,"E3"),sQuery(id+"F0.wireOp",EDGE,"E4"),sQuery(id+"F0.wireOp",EDGE,"E6")])]});
            var Q17;
            Q17=makeQuery(id+"F2.opExtrude","SWEPT_BODY",BODY,{"disambiguationData":[OSD([sQuery(id+"F0.wireOp",EDGE,"E0"),sQuery(id+"F0.wireOp",EDGE,"E1"),sQuery(id+"F0.wireOp",EDGE,"E5"),sQuery(id+"F0.wireOp",EDGE,"E7")])]});
            var Q18;
            Q18=makeQuery(id+"F9.opPattern","COPY",BODY,{"derivedFrom":makeQuery(id+"F1.opExtrude","SWEPT_BODY",BODY,{"disambiguationData":[OSD([sQuery(id+"F0.wireOp",EDGE,"E2"),sQuery(id+"F0.wireOp",EDGE,"E3"),sQuery(id+"F0.wireOp",EDGE,"E4"),sQuery(id+"F0.wireOp",EDGE,"E6")])]}),"instanceName":"1"});
            var Q19;
            Q19=makeQuery(id+"F9.opPattern","COPY",BODY,{"derivedFrom":makeQuery(id+"F2.opExtrude","SWEPT_BODY",BODY,{"disambiguationData":[OSD([sQuery(id+"F0.wireOp",EDGE,"E0"),sQuery(id+"F0.wireOp",EDGE,"E1"),sQuery(id+"F0.wireOp",EDGE,"E5"),sQuery(id+"F0.wireOp",EDGE,"E7")])]}),"instanceName":"1"});
            var Q20;
            Q20=makeQuery(id+"F10.opPattern","COPY",BODY,{"derivedFrom":makeQuery(id+"F1.opExtrude","SWEPT_BODY",BODY,{"disambiguationData":[OSD([sQuery(id+"F0.wireOp",EDGE,"E2"),sQuery(id+"F0.wireOp",EDGE,"E3"),sQuery(id+"F0.wireOp",EDGE,"E4"),sQuery(id+"F0.wireOp",EDGE,"E6")])]}),"instanceName":"1"});
            var Q21;
            Q21=makeQuery(id+"F10.opPattern","COPY",BODY,{"derivedFrom":makeQuery(id+"F2.opExtrude","SWEPT_BODY",BODY,{"disambiguationData":[OSD([sQuery(id+"F0.wireOp",EDGE,"E0"),sQuery(id+"F0.wireOp",EDGE,"E1"),sQuery(id+"F0.wireOp",EDGE,"E5"),sQuery(id+"F0.wireOp",EDGE,"E7")])]}),"instanceName":"1"});
            var Q22;
            Q22=makeQuery(id+"F10.opPattern","COPY",BODY,{"derivedFrom":makeQuery(id+"F9.opPattern","COPY",BODY,{"derivedFrom":makeQuery(id+"F1.opExtrude","SWEPT_BODY",BODY,{"disambiguationData":[OSD([sQuery(id+"F0.wireOp",EDGE,"E2"),sQuery(id+"F0.wireOp",EDGE,"E3"),sQuery(id+"F0.wireOp",EDGE,"E4"),sQuery(id+"F0.wireOp",EDGE,"E6")])]}),"instanceName":"1"}),"instanceName":"1"});
            var Q23;
            Q23=makeQuery(id+"F10.opPattern","COPY",BODY,{"derivedFrom":makeQuery(id+"F9.opPattern","COPY",BODY,{"derivedFrom":makeQuery(id+"F2.opExtrude","SWEPT_BODY",BODY,{"disambiguationData":[OSD([sQuery(id+"F0.wireOp",EDGE,"E0"),sQuery(id+"F0.wireOp",EDGE,"E1"),sQuery(id+"F0.wireOp",EDGE,"E5"),sQuery(id+"F0.wireOp",EDGE,"E7")])]}),"instanceName":"1"}),"instanceName":"1"});
            transform(context, id + "F11", {"entities" : qUnion([Q0, Q1, Q2, Q3, Q4, Q5, Q6, Q7, Q8, Q9, Q10, Q11, Q12, Q13, Q14, Q15, Q16, Q17, Q18, Q19, Q20, Q21, Q22, Q23]), "transformType" : TransformType.TRANSLATION_3D, "dx" : 0 * mm, "dy" : 203.2 * mm, "dz" : 0 * mm, "makeCopy" : true});
        }
        {
            var Q0;
            Q0=makeQuery(id+"F6.opExtrude","SWEPT_BODY",BODY,{"disambiguationData":[OSD([sQuery(id+"F0.wireOp",EDGE,"E8"),sQuery(id+"F0.wireOp",EDGE,"E9"),sQuery(id+"F0.wireOp",EDGE,"E11"),sQuery(id+"F0.wireOp",EDGE,"E12")])]});
            transform(context, id + "F12", {"entities" : qUnion([Q0]), "transformType" : TransformType.TRANSLATION_3D, "dx" : 0 * mm, "dy" : 406.4 * mm, "dz" : 0 * mm, "makeCopy" : true});
        }
    });
